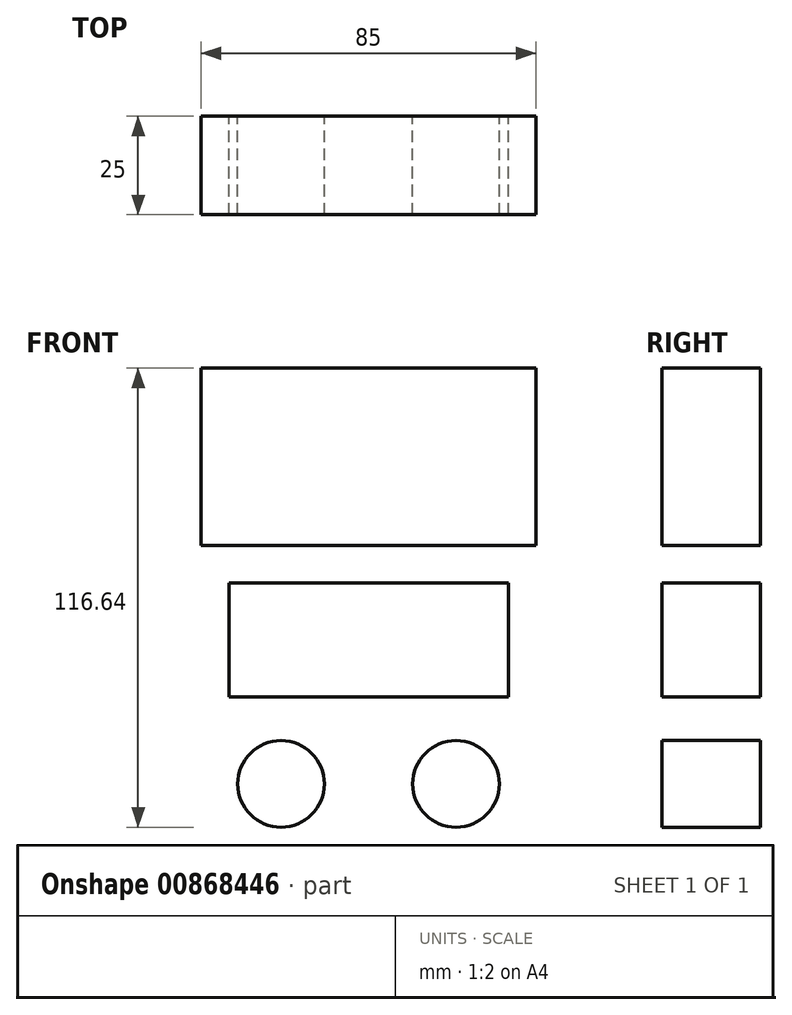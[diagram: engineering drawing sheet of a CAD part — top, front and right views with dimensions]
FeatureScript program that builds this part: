
annotation { "Feature Type Name" : "Feature", "Feature Type Description" : "" }
export const myFeature = defineFeature(function(context is Context, id is Id, definition is map)
    precondition{}
    {
        {
            var Q0;
            Q0=qCreatedBy(makeId("Front.planeOp"),FACE);
            var sketch = newSketch(context, id + "F0", { "sketchPlane" : qUnion([Q0])});
            skLineSegment(sketch, "E0.bottom", {"start": v(-73.52, 99.36) * mm, "end": v(11.48, 99.36) * mm});
            skLineSegment(sketch, "E0.top", {"start": v(-73.52, 54.36) * mm, "end": v(11.48, 54.36) * mm});
            skLineSegment(sketch, "E0.left", {"start": v(-73.52, 99.36) * mm, "end": v(-73.52, 54.36) * mm});
            skLineSegment(sketch, "E0.right", {"start": v(11.48, 99.36) * mm, "end": v(11.48, 54.36) * mm});
            skLineSegment(sketch, "E1.bottom", {"start": v(-66.52, 44.84) * mm, "end": v(4.48, 44.84) * mm});
            skLineSegment(sketch, "E1.top", {"start": v(-66.52, 15.84) * mm, "end": v(4.48, 15.84) * mm});
            skLineSegment(sketch, "E1.left", {"start": v(-66.52, 44.84) * mm, "end": v(-66.52, 15.84) * mm});
            skLineSegment(sketch, "E1.right", {"start": v(4.48, 44.84) * mm, "end": v(4.48, 15.84) * mm});
            skPoint(sketch, "E2", {"position": v(-31.02, 99.36) * mm});
            skPoint(sketch, "E3", {"position": v(-31.02, 54.36) * mm});
            skPoint(sketch, "E4", {"position": v(-31.02, 44.84) * mm});
            skPoint(sketch, "E5", {"position": v(-31.02, 15.84) * mm});
            skCircle(sketch, "E6", {"center": v(-53.24, -6.28) * mm, "radius": 11 * mm});
            skCircle(sketch, "E7", {"center": v(-8.8, -6.28) * mm, "radius": 11 * mm});
            skLineSegment(sketch, "E8", {"start": v(-53.24, -6.28) * mm, "end": v(-8.8, -6.28) * mm, "construction": true});
            skPoint(sketch, "E9", {"position": v(-31.02, -6.28) * mm});
            skLineSegment(sketch, "E10.0", {"start": v(-76.52, 102.36) * mm, "end": v(-76.52, 51.36) * mm, "construction": true});
            skLineSegment(sketch, "E10.1", {"start": v(-76.52, 102.36) * mm, "end": v(14.48, 102.36) * mm, "construction": true});
            skLineSegment(sketch, "E10.2", {"start": v(14.48, 102.36) * mm, "end": v(14.48, 51.36) * mm, "construction": true});
            skLineSegment(sketch, "E10.3", {"start": v(-76.52, 51.36) * mm, "end": v(14.48, 51.36) * mm, "construction": true});
            skLineSegment(sketch, "E11.0", {"start": v(-70.52, 48.84) * mm, "end": v(8.48, 48.84) * mm, "construction": true});
            skLineSegment(sketch, "E11.1", {"start": v(-70.52, 48.84) * mm, "end": v(-70.52, 11.84) * mm, "construction": true});
            skLineSegment(sketch, "E11.2", {"start": v(-70.52, 11.84) * mm, "end": v(8.48, 11.84) * mm, "construction": true});
            skLineSegment(sketch, "E11.3", {"start": v(8.48, 48.84) * mm, "end": v(8.48, 11.84) * mm, "construction": true});
            skCircle(sketch, "E12.0", {"center": v(-53.24, -6.28) * mm, "radius": 15 * mm, "construction": true});
            skCircle(sketch, "E13.0", {"center": v(-8.8, -6.28) * mm, "radius": 15 * mm, "construction": true});
            skSolve(sketch);
        }
        {
            var Q0;
            Q0 = qSketchRegion(id + "F0", true);
            extrude(context, id + "F1", {"entities" : qUnion([Q0]), "depth" : 25 * mm, "offsetDistance" : 25 * mm});
        }
    });
